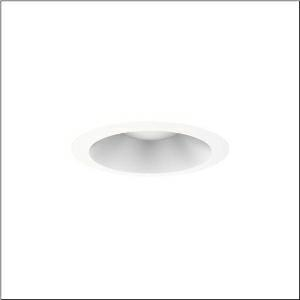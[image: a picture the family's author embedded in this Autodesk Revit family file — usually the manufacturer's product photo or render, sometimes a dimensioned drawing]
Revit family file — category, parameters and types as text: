
# Revit family: lunis_31-xl_51dn15mg32b
name_source: partatom
category: Lighting Fixtures
units: mm (PartAtom-declared; Revit-internal decimal feet)

## family parameters
Cut with Voids When Loaded = No
Host = Face
Light Source = No
Part Type = Normal
Room Calculation Point = No
Round Connector Dimension = Use Diameter
Shared = No

## types (1)
- --- (1 x LED, 2400 lm, 17 W, 3000K)
    Apparent Load = 17 VA
    CIE Flux Codes = 89 99 100 100 100
    Color Rendering = 80
    Color Temperature = 3000K
    Default Elevation = 1800 mm
    Description = Lunis 31-XL, downlight, light control with lens, light emission: direct distribution, LED rated luminous flux: 2.400lm, light colour: 830, mains connection: 220..240V, AC/DC, 0/50..60Hz, housing, of aluminium, white, protection rating (complete): IP20, protection rating (on room side): IP54, insulation class (complete): insulation class II (safety insulation), certification: CE, ENEC, packaging unit: 1 piece
    Height = 0 mm  [stored 0 ft]
    Lamp = 1 x LED
    Lamp Light Flux = 2400 lm
    Lamp Power = 17 W
    Lamp count = 1
    Length = 259 mm
    Luminous efficacy = 141 lm/W
    Manufacturer = Siteco
    ModVariant = No
    Model = 51DN15MG32B
    Mounting Place = Ceiling
    Mounting Type = Recessed
    Number of Poles = 1
    OnlyDefault = Yes
    Power Factor = 1
    Product Name = Lunis 31-XL
    Product group = downlight
    ProductGroupID = 401
    Protection Class = Protection class II
    Protection Degree = IP 20
    RLX_Detail_Level = 1
    RLX_Emergency_Light_Flux = 0 lm
    RLX_Emergency_Type = 0
    RLX_Emergency_Type_DB = No
    RlxData = <blob elided: 24341 chars, md5=60ed729e>
    Socket = socket
    Standby Power = 0 W
    System Light Flux = 2400 lm
    System Power = 17 W
    Type Comments = individual setting: luminous flux: 100 % | (ON | ON | ON | OFF) | 450 mA
    Type Image = l_1345915.jpg
    URL = http://relux.com
    VarID = @adj_029627
    Voltage = 0 V
    Weight = 0.00 kg
    Width = 0 mm  [stored 0 ft]

note: [stored X ft] marks values corroborated as IEEE doubles in the binary element streams (Revit-internal decimal feet)

## geometry (parser evidence)
native form markers: Blend x4, Sweep x10
no freeform markers — native parametric forms only
